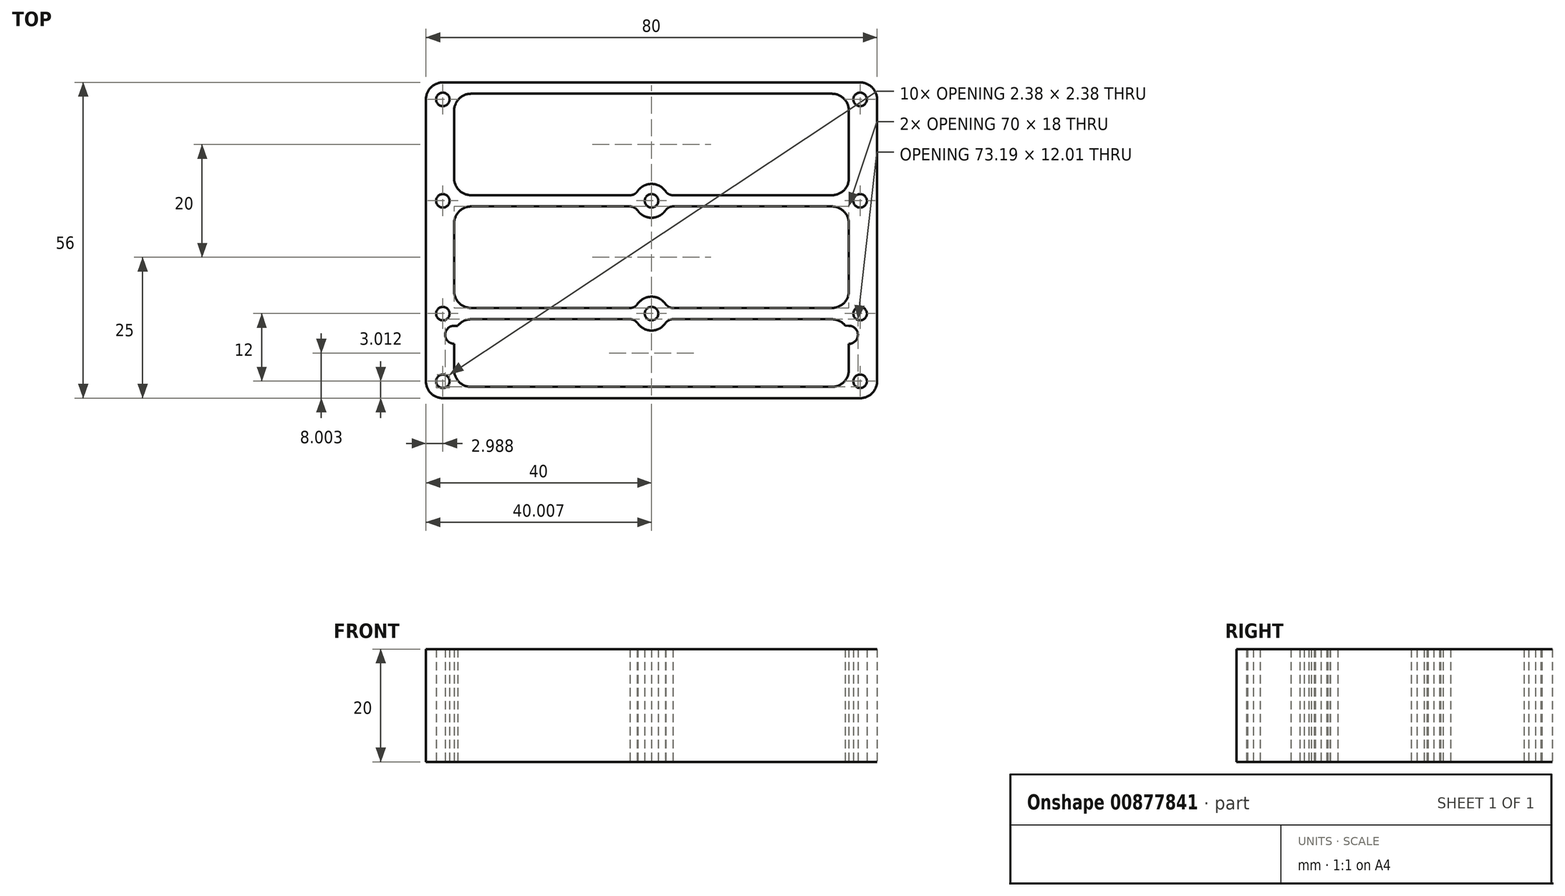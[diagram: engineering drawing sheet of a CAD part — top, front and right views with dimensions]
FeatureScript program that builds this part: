
annotation { "Feature Type Name" : "Feature", "Feature Type Description" : "" }
export const myFeature = defineFeature(function(context is Context, id is Id, definition is map)
    precondition{}
    {
        {
            var Q0;
            Q0=qCreatedBy(makeId("Top.planeOp"),FACE);
            var sketch = newSketch(context, id + "F0", { "sketchPlane" : qUnion([Q0])});
            skLineSegment(sketch, "E0", {"start": v(35, 3) * mm, "end": v(35, -9) * mm});
            skArc(sketch, "E1", {"start": v(35, -9) * mm, "mid": v(34.77, -10.15) * mm, "end": v(34.12, -11.12) * mm});
            skArc(sketch, "E2", {"start": v(34.12, -11.12) * mm, "mid": v(33.15, -11.77) * mm, "end": v(32, -12) * mm});
            skLineSegment(sketch, "E3", {"start": v(32, -12) * mm, "end": v(3.81, -12) * mm});
            skArc(sketch, "E4", {"start": v(3.81, -12) * mm, "mid": v(3.47, -11.96) * mm, "end": v(3.15, -11.85) * mm});
            skArc(sketch, "E5", {"start": v(3.15, -11.85) * mm, "mid": v(2.83, -11.65) * mm, "end": v(2.56, -11.4) * mm});
            skArc(sketch, "E6", {"start": v(2.56, -11.4) * mm, "mid": v(2.3, -11.1) * mm, "end": v(2.04, -10.81) * mm});
            skArc(sketch, "E7", {"start": v(2.04, -10.81) * mm, "mid": v(1.8, -10.61) * mm, "end": v(1.56, -10.43) * mm});
            skArc(sketch, "E8", {"start": v(1.56, -10.43) * mm, "mid": v(1.41, -10.33) * mm, "end": v(1.25, -10.25) * mm});
            skArc(sketch, "E9", {"start": v(1.25, -10.25) * mm, "mid": v(1.06, -10.18) * mm, "end": v(0.87, -10.11) * mm});
            skArc(sketch, "E10", {"start": v(0.87, -10.11) * mm, "mid": v(0.67, -10.06) * mm, "end": v(0.46, -10.03) * mm});
            skArc(sketch, "E11", {"start": v(0.46, -10.03) * mm, "mid": v(0.23, -10) * mm, "end": v(0, -10) * mm});
            skArc(sketch, "E12", {"start": v(0, -10) * mm, "mid": v(-0.72, -10.08) * mm, "end": v(-1.4, -10.34) * mm});
            skArc(sketch, "E13", {"start": v(-1.4, -10.34) * mm, "mid": v(-2.02, -10.77) * mm, "end": v(-2.52, -11.34) * mm});
            skArc(sketch, "E14", {"start": v(-2.52, -11.34) * mm, "mid": v(-2.75, -11.6) * mm, "end": v(-3.04, -11.81) * mm});
            skArc(sketch, "E15", {"start": v(-3.04, -11.81) * mm, "mid": v(-3.4, -11.95) * mm, "end": v(-3.8, -12) * mm});
            skLineSegment(sketch, "E16", {"start": v(-3.8, -12) * mm, "end": v(-32, -12) * mm});
            skArc(sketch, "E17", {"start": v(-32, -12) * mm, "mid": v(-33.15, -11.77) * mm, "end": v(-34.12, -11.12) * mm});
            skArc(sketch, "E18", {"start": v(-34.12, -11.12) * mm, "mid": v(-34.77, -10.15) * mm, "end": v(-35, -9) * mm});
            skLineSegment(sketch, "E19", {"start": v(-35, -9) * mm, "end": v(-35, 3) * mm});
            skArc(sketch, "E20", {"start": v(-35, 3) * mm, "mid": v(-34.77, 4.15) * mm, "end": v(-34.12, 5.12) * mm});
            skArc(sketch, "E21", {"start": v(-34.12, 5.12) * mm, "mid": v(-33.15, 5.77) * mm, "end": v(-32, 6) * mm});
            skLineSegment(sketch, "E22", {"start": v(-32, 6) * mm, "end": v(-3.8, 6) * mm});
            skArc(sketch, "E23", {"start": v(-3.8, 6) * mm, "mid": v(-3.43, 5.96) * mm, "end": v(-3.09, 5.82) * mm});
            skArc(sketch, "E24", {"start": v(-3.09, 5.82) * mm, "mid": v(-2.74, 5.59) * mm, "end": v(-2.45, 5.28) * mm});
            skArc(sketch, "E25", {"start": v(-2.45, 5.28) * mm, "mid": v(-2.26, 5.02) * mm, "end": v(-2.03, 4.79) * mm});
            skArc(sketch, "E26", {"start": v(-2.03, 4.79) * mm, "mid": v(-1.72, 4.55) * mm, "end": v(-1.38, 4.34) * mm});
            skArc(sketch, "E27", {"start": v(-1.38, 4.34) * mm, "mid": v(-1.06, 4.2) * mm, "end": v(-0.73, 4.1) * mm});
            skArc(sketch, "E28", {"start": v(-0.73, 4.1) * mm, "mid": v(-0.37, 4.03) * mm, "end": v(0, 4) * mm});
            skArc(sketch, "E29", {"start": v(0, 4) * mm, "mid": v(0.35, 4.02) * mm, "end": v(0.7, 4.08) * mm});
            skArc(sketch, "E30", {"start": v(0.7, 4.08) * mm, "mid": v(1.03, 4.19) * mm, "end": v(1.35, 4.33) * mm});
            skArc(sketch, "E31", {"start": v(1.35, 4.33) * mm, "mid": v(1.7, 4.53) * mm, "end": v(2, 4.77) * mm});
            skArc(sketch, "E32", {"start": v(2, 4.77) * mm, "mid": v(2.25, 5.01) * mm, "end": v(2.45, 5.28) * mm});
            skArc(sketch, "E33", {"start": v(2.45, 5.28) * mm, "mid": v(2.61, 5.47) * mm, "end": v(2.79, 5.64) * mm});
            skArc(sketch, "E34", {"start": v(2.79, 5.64) * mm, "mid": v(2.93, 5.75) * mm, "end": v(3.09, 5.84) * mm});
            skArc(sketch, "E35", {"start": v(3.09, 5.84) * mm, "mid": v(3.25, 5.9) * mm, "end": v(3.42, 5.96) * mm});
            skArc(sketch, "E36", {"start": v(3.42, 5.96) * mm, "mid": v(3.61, 5.99) * mm, "end": v(3.81, 6) * mm});
            skLineSegment(sketch, "E37", {"start": v(3.81, 6) * mm, "end": v(32, 6) * mm});
            skArc(sketch, "E38", {"start": v(32, 6) * mm, "mid": v(33.15, 5.77) * mm, "end": v(34.12, 5.12) * mm});
            skArc(sketch, "E39", {"start": v(34.12, 5.12) * mm, "mid": v(34.77, 4.15) * mm, "end": v(35, 3) * mm});
            skLineSegment(sketch, "E40", {"start": v(35, 3) * mm, "end": v(35, 3) * mm});
            skLineSegment(sketch, "E41", {"start": v(35, 23) * mm, "end": v(35, 11) * mm});
            skArc(sketch, "E42", {"start": v(35, 11) * mm, "mid": v(34.77, 9.85) * mm, "end": v(34.12, 8.88) * mm});
            skArc(sketch, "E43", {"start": v(34.12, 8.88) * mm, "mid": v(33.15, 8.23) * mm, "end": v(32, 8) * mm});
            skLineSegment(sketch, "E44", {"start": v(32, 8) * mm, "end": v(3.81, 8) * mm});
            skArc(sketch, "E45", {"start": v(3.81, 8) * mm, "mid": v(3.42, 8.05) * mm, "end": v(3.06, 8.18) * mm});
            skArc(sketch, "E46", {"start": v(3.06, 8.18) * mm, "mid": v(2.75, 8.4) * mm, "end": v(2.5, 8.68) * mm});
            skArc(sketch, "E47", {"start": v(2.5, 8.68) * mm, "mid": v(2.03, 9.23) * mm, "end": v(1.43, 9.64) * mm});
            skArc(sketch, "E48", {"start": v(1.43, 9.64) * mm, "mid": v(0.74, 9.91) * mm, "end": v(0, 10) * mm});
            skArc(sketch, "E49", {"start": v(0, 10) * mm, "mid": v(-0.37, 9.98) * mm, "end": v(-0.73, 9.91) * mm});
            skArc(sketch, "E50", {"start": v(-0.73, 9.91) * mm, "mid": v(-1.1, 9.8) * mm, "end": v(-1.44, 9.64) * mm});
            skArc(sketch, "E51", {"start": v(-1.44, 9.64) * mm, "mid": v(-1.77, 9.44) * mm, "end": v(-2.06, 9.2) * mm});
            skArc(sketch, "E52", {"start": v(-2.06, 9.2) * mm, "mid": v(-2.3, 8.95) * mm, "end": v(-2.5, 8.67) * mm});
            skArc(sketch, "E53", {"start": v(-2.5, 8.67) * mm, "mid": v(-2.65, 8.5) * mm, "end": v(-2.81, 8.35) * mm});
            skArc(sketch, "E54", {"start": v(-2.81, 8.35) * mm, "mid": v(-2.96, 8.24) * mm, "end": v(-3.13, 8.14) * mm});
            skArc(sketch, "E55", {"start": v(-3.13, 8.14) * mm, "mid": v(-3.24, 8.1) * mm, "end": v(-3.36, 8.06) * mm});
            skArc(sketch, "E56", {"start": v(-3.36, 8.06) * mm, "mid": v(-3.58, 8.02) * mm, "end": v(-3.8, 8) * mm});
            skLineSegment(sketch, "E57", {"start": v(-3.8, 8) * mm, "end": v(-32, 8) * mm});
            skArc(sketch, "E58", {"start": v(-32, 8) * mm, "mid": v(-33.15, 8.23) * mm, "end": v(-34.12, 8.88) * mm});
            skArc(sketch, "E59", {"start": v(-34.12, 8.88) * mm, "mid": v(-34.77, 9.85) * mm, "end": v(-35, 11) * mm});
            skLineSegment(sketch, "E60", {"start": v(-35, 11) * mm, "end": v(-35, 23) * mm});
            skArc(sketch, "E61", {"start": v(-35, 23) * mm, "mid": v(-34.77, 24.15) * mm, "end": v(-34.12, 25.12) * mm});
            skArc(sketch, "E62", {"start": v(-34.12, 25.12) * mm, "mid": v(-33.15, 25.77) * mm, "end": v(-32, 26) * mm});
            skLineSegment(sketch, "E63", {"start": v(-32, 26) * mm, "end": v(-3.8, 26) * mm});
            skLineSegment(sketch, "E64", {"start": v(-3.8, 26) * mm, "end": v(-2.35, 26) * mm});
            skLineSegment(sketch, "E65", {"start": v(-2.35, 26) * mm, "end": v(-0.17, 26) * mm});
            skLineSegment(sketch, "E66", {"start": v(-0.17, 26) * mm, "end": v(2.63, 26) * mm});
            skLineSegment(sketch, "E67", {"start": v(2.63, 26) * mm, "end": v(3.93, 26) * mm});
            skLineSegment(sketch, "E68", {"start": v(3.93, 26) * mm, "end": v(32, 26) * mm});
            skArc(sketch, "E69", {"start": v(32, 26) * mm, "mid": v(33.15, 25.77) * mm, "end": v(34.12, 25.12) * mm});
            skArc(sketch, "E70", {"start": v(34.12, 25.12) * mm, "mid": v(34.77, 24.15) * mm, "end": v(35, 23) * mm});
            skLineSegment(sketch, "E71", {"start": v(35, 23) * mm, "end": v(35, 23) * mm});
            skArc(sketch, "E72", {"start": v(36.6, -16.75) * mm, "mid": v(36.48, -17.36) * mm, "end": v(36.14, -17.88) * mm});
            skArc(sketch, "E73", {"start": v(36.14, -17.88) * mm, "mid": v(35.62, -18.24) * mm, "end": v(35, -18.37) * mm});
            skLineSegment(sketch, "E74", {"start": v(35, -18.37) * mm, "end": v(35, -23) * mm});
            skArc(sketch, "E75", {"start": v(35, -23) * mm, "mid": v(34.77, -24.15) * mm, "end": v(34.12, -25.12) * mm});
            skArc(sketch, "E76", {"start": v(34.12, -25.12) * mm, "mid": v(33.15, -25.77) * mm, "end": v(32, -26) * mm});
            skLineSegment(sketch, "E77", {"start": v(32, -26) * mm, "end": v(-32, -26) * mm});
            skArc(sketch, "E78", {"start": v(-32, -26) * mm, "mid": v(-33.15, -25.77) * mm, "end": v(-34.12, -25.12) * mm});
            skArc(sketch, "E79", {"start": v(-34.12, -25.12) * mm, "mid": v(-34.77, -24.15) * mm, "end": v(-35, -23) * mm});
            skLineSegment(sketch, "E80", {"start": v(-35, -23) * mm, "end": v(-35, -18.35) * mm});
            skArc(sketch, "E81", {"start": v(-35, -18.35) * mm, "mid": v(-35.6, -18.23) * mm, "end": v(-36.12, -17.89) * mm});
            skArc(sketch, "E82", {"start": v(-36.12, -17.89) * mm, "mid": v(-36.46, -17.37) * mm, "end": v(-36.59, -16.75) * mm});
            skArc(sketch, "E83", {"start": v(-36.59, -16.75) * mm, "mid": v(-36.46, -16.13) * mm, "end": v(-36.11, -15.61) * mm});
            skArc(sketch, "E84", {"start": v(-36.11, -15.61) * mm, "mid": v(-35.6, -15.27) * mm, "end": v(-35, -15.15) * mm});
            skLineSegment(sketch, "E85", {"start": v(-35, -15.15) * mm, "end": v(-34.37, -15.15) * mm});
            skArc(sketch, "E86", {"start": v(-34.37, -15.15) * mm, "mid": v(-33.88, -14.66) * mm, "end": v(-33.3, -14.3) * mm});
            skArc(sketch, "E87", {"start": v(-33.3, -14.3) * mm, "mid": v(-32.66, -14.07) * mm, "end": v(-32, -14) * mm});
            skLineSegment(sketch, "E88", {"start": v(-32, -14) * mm, "end": v(-3.8, -14) * mm});
            skArc(sketch, "E89", {"start": v(-3.8, -14) * mm, "mid": v(-3.59, -14) * mm, "end": v(-3.38, -14.05) * mm});
            skArc(sketch, "E90", {"start": v(-3.38, -14.05) * mm, "mid": v(-3.2, -14.1) * mm, "end": v(-3.02, -14.2) * mm});
            skArc(sketch, "E91", {"start": v(-3.02, -14.2) * mm, "mid": v(-2.9, -14.27) * mm, "end": v(-2.78, -14.37) * mm});
            skArc(sketch, "E92", {"start": v(-2.78, -14.37) * mm, "mid": v(-2.6, -14.55) * mm, "end": v(-2.44, -14.74) * mm});
            skArc(sketch, "E93", {"start": v(-2.44, -14.74) * mm, "mid": v(-1.95, -15.27) * mm, "end": v(-1.35, -15.68) * mm});
            skArc(sketch, "E94", {"start": v(-1.35, -15.68) * mm, "mid": v(-0.7, -15.92) * mm, "end": v(0, -16) * mm});
            skArc(sketch, "E95", {"start": v(0, -16) * mm, "mid": v(0.72, -15.92) * mm, "end": v(1.4, -15.66) * mm});
            skArc(sketch, "E96", {"start": v(1.4, -15.66) * mm, "mid": v(1.98, -15.25) * mm, "end": v(2.45, -14.7) * mm});
            skArc(sketch, "E97", {"start": v(2.45, -14.7) * mm, "mid": v(2.74, -14.4) * mm, "end": v(3.09, -14.17) * mm});
            skArc(sketch, "E98", {"start": v(3.09, -14.17) * mm, "mid": v(3.44, -14.04) * mm, "end": v(3.8, -14) * mm});
            skLineSegment(sketch, "E99", {"start": v(3.8, -14) * mm, "end": v(32, -14) * mm});
            skArc(sketch, "E100", {"start": v(32, -14) * mm, "mid": v(32.67, -14.08) * mm, "end": v(33.3, -14.3) * mm});
            skArc(sketch, "E101", {"start": v(33.3, -14.3) * mm, "mid": v(33.88, -14.66) * mm, "end": v(34.36, -15.15) * mm});
            skLineSegment(sketch, "E102", {"start": v(34.36, -15.15) * mm, "end": v(35, -15.15) * mm});
            skArc(sketch, "E103", {"start": v(35, -15.15) * mm, "mid": v(35.62, -15.27) * mm, "end": v(36.14, -15.62) * mm});
            skArc(sketch, "E104", {"start": v(36.14, -15.62) * mm, "mid": v(36.48, -16.14) * mm, "end": v(36.6, -16.75) * mm});
            skLineSegment(sketch, "E105", {"start": v(36.6, -16.75) * mm, "end": v(36.6, -16.75) * mm});
            skArc(sketch, "E106", {"start": v(35.8, 25) * mm, "mid": v(36.15, 25.85) * mm, "end": v(37, 26.2) * mm});
            skArc(sketch, "E107", {"start": v(37, 26.2) * mm, "mid": v(37.85, 25.85) * mm, "end": v(38.2, 25) * mm});
            skArc(sketch, "E108", {"start": v(38.2, 25) * mm, "mid": v(37.85, 24.15) * mm, "end": v(37, 23.8) * mm});
            skArc(sketch, "E109", {"start": v(37, 23.8) * mm, "mid": v(36.15, 24.15) * mm, "end": v(35.8, 25) * mm});
            skLineSegment(sketch, "E110", {"start": v(35.8, 25) * mm, "end": v(35.8, 25) * mm});
            skArc(sketch, "E111", {"start": v(35.8, -25) * mm, "mid": v(36.15, -24.15) * mm, "end": v(37, -23.8) * mm});
            skArc(sketch, "E112", {"start": v(37, -23.8) * mm, "mid": v(37.85, -24.15) * mm, "end": v(38.2, -25) * mm});
            skArc(sketch, "E113", {"start": v(38.2, -25) * mm, "mid": v(37.85, -25.85) * mm, "end": v(37, -26.2) * mm});
            skArc(sketch, "E114", {"start": v(37, -26.2) * mm, "mid": v(36.15, -25.85) * mm, "end": v(35.8, -25) * mm});
            skLineSegment(sketch, "E115", {"start": v(35.8, -25) * mm, "end": v(35.8, -25) * mm});
            skArc(sketch, "E116", {"start": v(-38.2, -25) * mm, "mid": v(-37.85, -24.15) * mm, "end": v(-37, -23.8) * mm});
            skArc(sketch, "E117", {"start": v(-37, -23.8) * mm, "mid": v(-36.15, -24.15) * mm, "end": v(-35.8, -25) * mm});
            skArc(sketch, "E118", {"start": v(-35.8, -25) * mm, "mid": v(-36.15, -25.85) * mm, "end": v(-37, -26.2) * mm});
            skArc(sketch, "E119", {"start": v(-37, -26.2) * mm, "mid": v(-37.85, -25.85) * mm, "end": v(-38.2, -25) * mm});
            skLineSegment(sketch, "E120", {"start": v(-38.2, -25) * mm, "end": v(-38.2, -25) * mm});
            skArc(sketch, "E121", {"start": v(-38.2, 25) * mm, "mid": v(-37.85, 25.85) * mm, "end": v(-37, 26.2) * mm});
            skArc(sketch, "E122", {"start": v(-37, 26.2) * mm, "mid": v(-36.15, 25.85) * mm, "end": v(-35.8, 25) * mm});
            skArc(sketch, "E123", {"start": v(-35.8, 25) * mm, "mid": v(-36.15, 24.15) * mm, "end": v(-37, 23.8) * mm});
            skArc(sketch, "E124", {"start": v(-37, 23.8) * mm, "mid": v(-37.85, 24.15) * mm, "end": v(-38.2, 25) * mm});
            skLineSegment(sketch, "E125", {"start": v(-38.2, 25) * mm, "end": v(-38.2, 25) * mm});
            skArc(sketch, "E126", {"start": v(-1.2, -13) * mm, "mid": v(-0.85, -12.15) * mm, "end": v(0, -11.8) * mm});
            skArc(sketch, "E127", {"start": v(0, -11.8) * mm, "mid": v(0.85, -12.15) * mm, "end": v(1.2, -13) * mm});
            skArc(sketch, "E128", {"start": v(1.2, -13) * mm, "mid": v(0.85, -13.85) * mm, "end": v(0, -14.2) * mm});
            skArc(sketch, "E129", {"start": v(0, -14.2) * mm, "mid": v(-0.85, -13.85) * mm, "end": v(-1.2, -13) * mm});
            skLineSegment(sketch, "E130", {"start": v(-1.2, -13) * mm, "end": v(-1.2, -13) * mm});
            skArc(sketch, "E131", {"start": v(-1.2, 7) * mm, "mid": v(-0.85, 7.85) * mm, "end": v(0, 8.2) * mm});
            skArc(sketch, "E132", {"start": v(0, 8.2) * mm, "mid": v(0.85, 7.85) * mm, "end": v(1.2, 7) * mm});
            skArc(sketch, "E133", {"start": v(1.2, 7) * mm, "mid": v(0.85, 6.15) * mm, "end": v(0, 5.8) * mm});
            skArc(sketch, "E134", {"start": v(0, 5.8) * mm, "mid": v(-0.85, 6.15) * mm, "end": v(-1.2, 7) * mm});
            skLineSegment(sketch, "E135", {"start": v(-1.2, 7) * mm, "end": v(-1.2, 7) * mm});
            skLineSegment(sketch, "E136", {"start": v(-40, -25) * mm, "end": v(-40, 25) * mm});
            skArc(sketch, "E137", {"start": v(-40, 25) * mm, "mid": v(-39.77, 26.15) * mm, "end": v(-39.12, 27.12) * mm});
            skArc(sketch, "E138", {"start": v(-39.12, 27.12) * mm, "mid": v(-38.15, 27.77) * mm, "end": v(-37, 28) * mm});
            skLineSegment(sketch, "E139", {"start": v(-37, 28) * mm, "end": v(37, 28) * mm});
            skArc(sketch, "E140", {"start": v(37, 28) * mm, "mid": v(38.15, 27.77) * mm, "end": v(39.12, 27.12) * mm});
            skArc(sketch, "E141", {"start": v(39.12, 27.12) * mm, "mid": v(39.77, 26.15) * mm, "end": v(40, 25) * mm});
            skLineSegment(sketch, "E142", {"start": v(40, 25) * mm, "end": v(40, -25) * mm});
            skArc(sketch, "E143", {"start": v(40, -25) * mm, "mid": v(39.77, -26.15) * mm, "end": v(39.12, -27.12) * mm});
            skArc(sketch, "E144", {"start": v(39.12, -27.12) * mm, "mid": v(38.15, -27.77) * mm, "end": v(37, -28) * mm});
            skLineSegment(sketch, "E145", {"start": v(37, -28) * mm, "end": v(-37, -28) * mm});
            skArc(sketch, "E146", {"start": v(-37, -28) * mm, "mid": v(-38.15, -27.77) * mm, "end": v(-39.12, -27.12) * mm});
            skArc(sketch, "E147", {"start": v(-39.12, -27.12) * mm, "mid": v(-39.77, -26.15) * mm, "end": v(-40, -25) * mm});
            skLineSegment(sketch, "E148", {"start": v(-40, -25) * mm, "end": v(-40, -25) * mm});
            skArc(sketch, "E149", {"start": v(35.8, 7) * mm, "mid": v(36.15, 7.85) * mm, "end": v(37, 8.2) * mm});
            skArc(sketch, "E150", {"start": v(37, 8.2) * mm, "mid": v(37.85, 7.85) * mm, "end": v(38.2, 7) * mm});
            skArc(sketch, "E151", {"start": v(38.2, 7) * mm, "mid": v(37.85, 6.15) * mm, "end": v(37, 5.8) * mm});
            skArc(sketch, "E152", {"start": v(37, 5.8) * mm, "mid": v(36.15, 6.15) * mm, "end": v(35.8, 7) * mm});
            skLineSegment(sketch, "E153", {"start": v(35.8, 7) * mm, "end": v(35.8, 7) * mm});
            skArc(sketch, "E154", {"start": v(-38.2, 7) * mm, "mid": v(-37.85, 7.85) * mm, "end": v(-37, 8.2) * mm});
            skArc(sketch, "E155", {"start": v(-37, 8.2) * mm, "mid": v(-36.15, 7.85) * mm, "end": v(-35.8, 7) * mm});
            skArc(sketch, "E156", {"start": v(-35.8, 7) * mm, "mid": v(-36.15, 6.15) * mm, "end": v(-37, 5.8) * mm});
            skArc(sketch, "E157", {"start": v(-37, 5.8) * mm, "mid": v(-37.85, 6.15) * mm, "end": v(-38.2, 7) * mm});
            skLineSegment(sketch, "E158", {"start": v(-38.2, 7) * mm, "end": v(-38.2, 7) * mm});
            skArc(sketch, "E159", {"start": v(35.8, -13) * mm, "mid": v(36.15, -12.15) * mm, "end": v(37, -11.8) * mm});
            skArc(sketch, "E160", {"start": v(37, -11.8) * mm, "mid": v(37.85, -12.15) * mm, "end": v(38.2, -13) * mm});
            skArc(sketch, "E161", {"start": v(38.2, -13) * mm, "mid": v(37.85, -13.85) * mm, "end": v(37, -14.2) * mm});
            skArc(sketch, "E162", {"start": v(37, -14.2) * mm, "mid": v(36.15, -13.85) * mm, "end": v(35.8, -13) * mm});
            skLineSegment(sketch, "E163", {"start": v(35.8, -13) * mm, "end": v(35.8, -13) * mm});
            skArc(sketch, "E164", {"start": v(-38.2, -13) * mm, "mid": v(-37.85, -12.15) * mm, "end": v(-37, -11.8) * mm});
            skArc(sketch, "E165", {"start": v(-37, -11.8) * mm, "mid": v(-36.15, -12.15) * mm, "end": v(-35.8, -13) * mm});
            skArc(sketch, "E166", {"start": v(-35.8, -13) * mm, "mid": v(-36.15, -13.85) * mm, "end": v(-37, -14.2) * mm});
            skArc(sketch, "E167", {"start": v(-37, -14.2) * mm, "mid": v(-37.85, -13.85) * mm, "end": v(-38.2, -13) * mm});
            skLineSegment(sketch, "E168", {"start": v(-38.2, -13) * mm, "end": v(-38.2, -13) * mm});
            skSolve(sketch);
        }
        {
            var Q0;
            Q0 = qSketchRegion(id + "F0", true);
            extrude(context, id + "F1", {"entities" : qUnion([Q0]), "depth" : 20 * mm, "offsetDistance" : 25 * mm});
        }
    });
